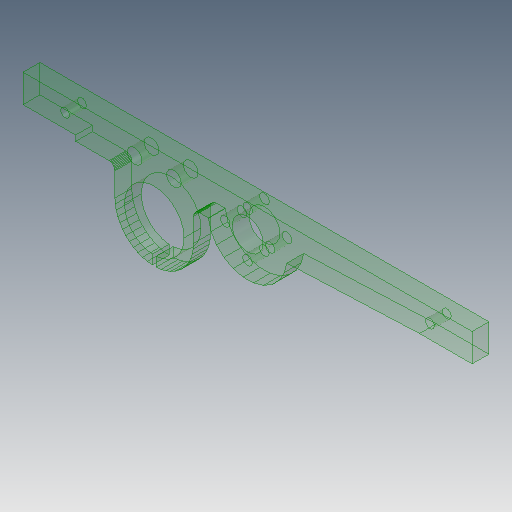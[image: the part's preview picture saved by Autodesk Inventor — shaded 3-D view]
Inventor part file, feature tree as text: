
AUTODESK INVENTOR PART (.ipt)
format: ipt  version: 2017 (Build 210142000, 142)  size: 290,816 bytes
history: native  units: mm
features: sketch x8, other x3
ambient origin geometry x8: Origin, YZ Plane, XZ Plane, XY Plane, X Axis, Y Axis, Z Axis, Center Point
bodies: Solid1 (feature_tree)
feature tree (11):
  other  "Rear-Bed-Holder-mid.ipt"
  other  "Solid1::Rear-Bed-Holder-mid.ipt"
  other  "TaggingFeature1"
  sketch  "Sketch1"  dims[d0=10.0mm]
  sketch  "Sketch2"
  sketch  "Sketch3"
  sketch  "Sketch4"
  sketch  "Sketch5"
  sketch  "Sketch6"
  sketch  "Sketch7"
  sketch  "Sketch8"
